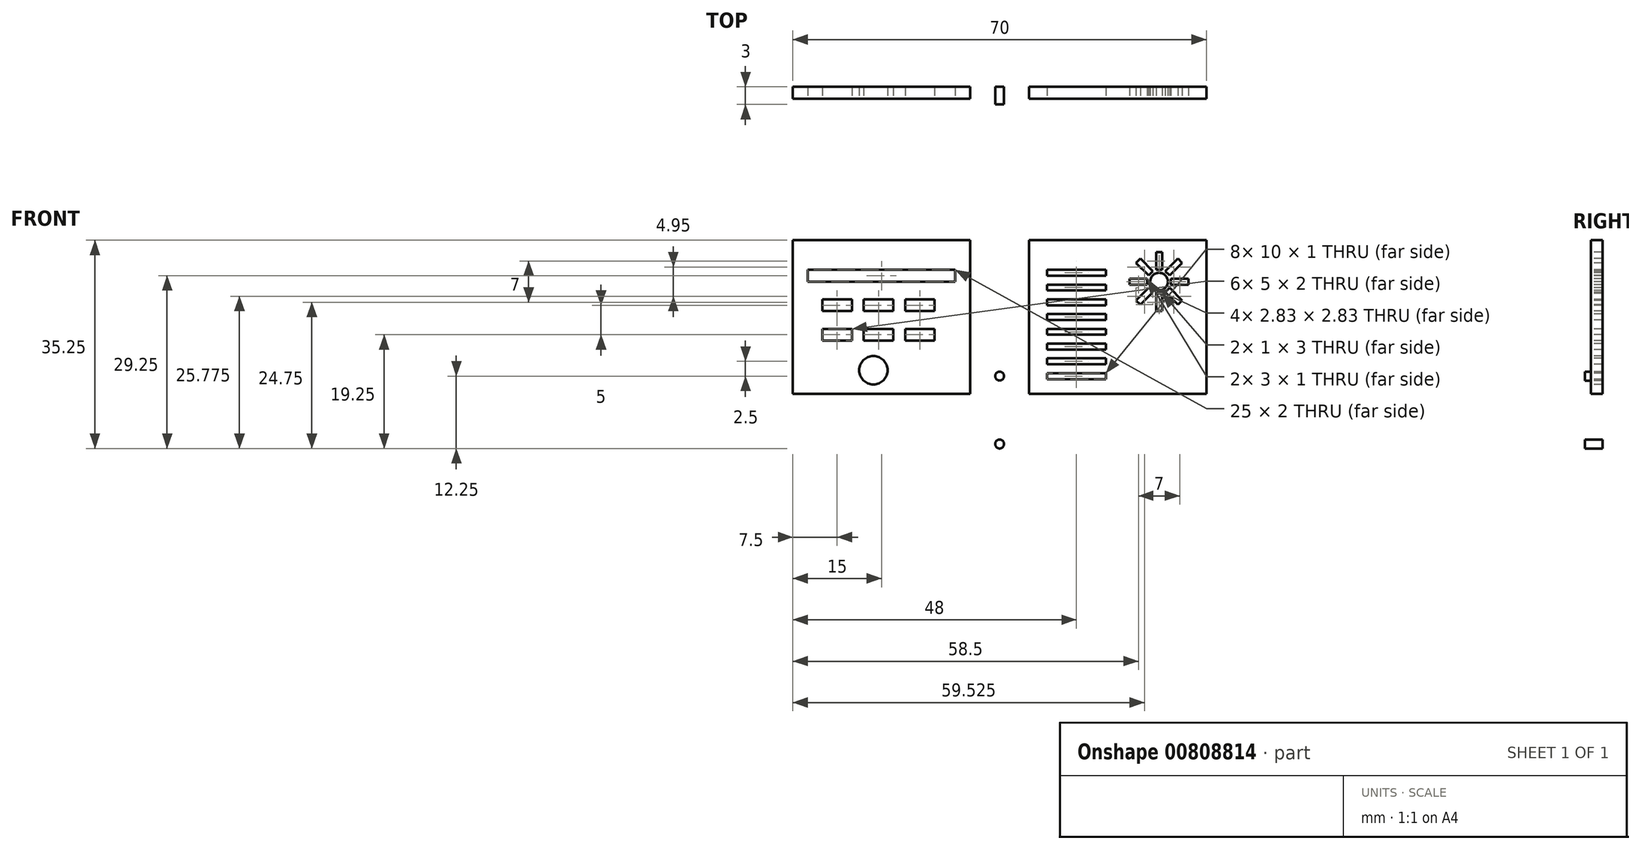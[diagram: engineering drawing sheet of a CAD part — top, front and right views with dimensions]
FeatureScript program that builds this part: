
annotation { "Feature Type Name" : "Feature", "Feature Type Description" : "" }
export const myFeature = defineFeature(function(context is Context, id is Id, definition is map)
    precondition{}
    {
        {
            var Q0;
            Q0=qCreatedBy(makeId("Front.planeOp"),FACE);
            var sketch = newSketch(context, id + "F0", { "sketchPlane" : qUnion([Q0])});
            skLineSegment(sketch, "E0.bottom", {"start": v(-55, 50) * mm, "end": v(55, 50) * mm});
            skLineSegment(sketch, "E0.top", {"start": v(-55, -50) * mm, "end": v(55, -50) * mm});
            skPoint(sketch, "E0.middle", {"position": v(0, 0) * mm});
            skLineSegment(sketch, "E1.bottom", {"start": v(5, 53) * mm, "end": v(-5, 53) * mm});
            skLineSegment(sketch, "E1.top", {"start": v(5, 47) * mm, "end": v(-5, 47) * mm});
            skLineSegment(sketch, "E1.left", {"start": v(5, 53) * mm, "end": v(5, 47) * mm});
            skLineSegment(sketch, "E1.right", {"start": v(-5, 53) * mm, "end": v(-5, 47) * mm});
            skPoint(sketch, "E1.middle", {"position": v(0, 50) * mm});
            skLineSegment(sketch, "E2.bottom", {"start": v(-25, 47) * mm, "end": v(-35, 47) * mm});
            skLineSegment(sketch, "E2.top", {"start": v(-25, 53) * mm, "end": v(-35, 53) * mm});
            skLineSegment(sketch, "E2.left", {"start": v(-25, 47) * mm, "end": v(-25, 53) * mm});
            skLineSegment(sketch, "E2.right", {"start": v(-35, 47) * mm, "end": v(-35, 53) * mm});
            skPoint(sketch, "E2.middle", {"position": v(-30, 50) * mm});
            skLineSegment(sketch, "E3.bottom", {"start": v(25, 47) * mm, "end": v(35, 47) * mm});
            skLineSegment(sketch, "E3.top", {"start": v(25, 53) * mm, "end": v(35, 53) * mm});
            skLineSegment(sketch, "E3.left", {"start": v(25, 47) * mm, "end": v(25, 53) * mm});
            skLineSegment(sketch, "E3.right", {"start": v(35, 47) * mm, "end": v(35, 53) * mm});
            skPoint(sketch, "E3.middle", {"position": v(30, 50) * mm});
            skPoint(sketch, "E4.center", {"position": v(-2.67, -2.67) * mm});
            skLineSegment(sketch, "E5", {"start": v(0, 0) * mm, "end": v(18.8, 0) * mm});
            skLineSegment(sketch, "E6", {"start": v(-55, 50) * mm, "end": v(-55, -50) * mm});
            skLineSegment(sketch, "E7", {"start": v(55, -50) * mm, "end": v(55, 50) * mm});
            skLineSegment(sketch, "E8.bottom", {"start": v(-58, 5) * mm, "end": v(-52, 5) * mm});
            skLineSegment(sketch, "E8.top", {"start": v(-58, -5) * mm, "end": v(-52, -5) * mm});
            skLineSegment(sketch, "E8.left", {"start": v(-58, 5) * mm, "end": v(-58, -5) * mm});
            skLineSegment(sketch, "E8.right", {"start": v(-52, 5) * mm, "end": v(-52, -5) * mm});
            skPoint(sketch, "E8.middle", {"position": v(-55, 0) * mm});
            skLineSegment(sketch, "E9.bottom", {"start": v(58, 5) * mm, "end": v(52, 5) * mm});
            skLineSegment(sketch, "E9.top", {"start": v(58, -5) * mm, "end": v(52, -5) * mm});
            skLineSegment(sketch, "E9.left", {"start": v(58, 5) * mm, "end": v(58, -5) * mm});
            skLineSegment(sketch, "E9.right", {"start": v(52, 5) * mm, "end": v(52, -5) * mm});
            skPoint(sketch, "E9.middle", {"position": v(55, 0) * mm});
            skLineSegment(sketch, "E10.0.1.0", {"start": v(-52, 35) * mm, "end": v(-52, 25) * mm});
            skLineSegment(sketch, "E10.0.1.1", {"start": v(-58, 35) * mm, "end": v(-52, 35) * mm});
            skLineSegment(sketch, "E10.0.1.2", {"start": v(-58, 35) * mm, "end": v(-58, 25) * mm});
            skLineSegment(sketch, "E10.0.1.3", {"start": v(-58, 25) * mm, "end": v(-52, 25) * mm});
            skLineSegment(sketch, "E10.0.1.4", {"start": v(58, 25) * mm, "end": v(52, 25) * mm});
            skLineSegment(sketch, "E10.0.1.5", {"start": v(58, 35) * mm, "end": v(58, 25) * mm});
            skLineSegment(sketch, "E10.0.1.6", {"start": v(58, 35) * mm, "end": v(52, 35) * mm});
            skLineSegment(sketch, "E10.0.1.7", {"start": v(52, 35) * mm, "end": v(52, 25) * mm});
            skLineSegment(sketch, "E10.direction1", {"start": v(-52, -5) * mm, "end": v(-27, -5) * mm, "construction": true});
            skLineSegment(sketch, "E11.0.1.0", {"start": v(-52, -25) * mm, "end": v(-52, -35) * mm});
            skLineSegment(sketch, "E11.0.1.1", {"start": v(-58, -25) * mm, "end": v(-52, -25) * mm});
            skLineSegment(sketch, "E11.0.1.2", {"start": v(-58, -25) * mm, "end": v(-58, -35) * mm});
            skLineSegment(sketch, "E11.0.1.3", {"start": v(-58, -35) * mm, "end": v(-52, -35) * mm});
            skLineSegment(sketch, "E11.0.1.4", {"start": v(58, -35) * mm, "end": v(52, -35) * mm});
            skLineSegment(sketch, "E11.0.1.5", {"start": v(58, -25) * mm, "end": v(58, -35) * mm});
            skLineSegment(sketch, "E11.0.1.6", {"start": v(58, -25) * mm, "end": v(52, -25) * mm});
            skLineSegment(sketch, "E11.0.1.7", {"start": v(52, -25) * mm, "end": v(52, -35) * mm});
            skLineSegment(sketch, "E11.direction2", {"start": v(-52, -5) * mm, "end": v(-52, -35) * mm, "construction": true});
            skLineSegment(sketch, "E12.MirrorCS", {"start": v(-25, -47) * mm, "end": v(-35, -47) * mm});
            skLineSegment(sketch, "E13.MirrorCS", {"start": v(-35, -47) * mm, "end": v(-35, -53) * mm});
            skLineSegment(sketch, "E14.MirrorCS", {"start": v(-25, -53) * mm, "end": v(-35, -53) * mm});
            skLineSegment(sketch, "E15.MirrorCS", {"start": v(-25, -47) * mm, "end": v(-25, -53) * mm});
            skLineSegment(sketch, "E16.MirrorCS", {"start": v(-5, -53) * mm, "end": v(-5, -47) * mm});
            skLineSegment(sketch, "E17.MirrorCS", {"start": v(5, -53) * mm, "end": v(-5, -53) * mm});
            skLineSegment(sketch, "E18.MirrorCS", {"start": v(5, -47) * mm, "end": v(-5, -47) * mm});
            skLineSegment(sketch, "E19.MirrorCS", {"start": v(5, -53) * mm, "end": v(5, -47) * mm});
            skLineSegment(sketch, "E20.MirrorCS", {"start": v(35, -47) * mm, "end": v(35, -53) * mm});
            skLineSegment(sketch, "E21.MirrorCS", {"start": v(25, -53) * mm, "end": v(35, -53) * mm});
            skLineSegment(sketch, "E22.MirrorCS", {"start": v(25, -47) * mm, "end": v(35, -47) * mm});
            skLineSegment(sketch, "E23.MirrorCS", {"start": v(25, -47) * mm, "end": v(25, -53) * mm});
            skSolve(sketch);
        }
        {
            var Q0;
            {var subQ5=sQuery(id+"F0.wireOp",EDGE,"E2.top");Q0=makeQuery(id+"F0.imprint","IMPRINT",FACE,{"disambiguationData":[TD([[makeQuery(id+"F0.imprint","IMPRINT",EDGE,{"derivedFrom":subQ5}),1.0]])]});}
            var Q1;
            {var subQ5=sQuery(id+"F0.wireOp",EDGE,"E1.bottom");Q1=makeQuery(id+"F0.imprint","IMPRINT",FACE,{"disambiguationData":[TD([[makeQuery(id+"F0.imprint","IMPRINT",EDGE,{"derivedFrom":subQ5}),1.0]])]});}
            var Q2;
            {var subQ5=sQuery(id+"F0.wireOp",EDGE,"E3.top");Q2=makeQuery(id+"F0.imprint","IMPRINT",FACE,{"disambiguationData":[TD([[makeQuery(id+"F0.imprint","IMPRINT",EDGE,{"derivedFrom":subQ5}),-1.0]])]});}
            var Q3;
            {var subQ5=sQuery(id+"F0.wireOp",EDGE,"E4.2.10");Q3=makeQuery(id+"F0.imprint","IMPRINT",FACE,{"disambiguationData":[TD([[makeQuery(id+"F0.imprint","IMPRINT",EDGE,{"derivedFrom":subQ5}),-1.0]])]});}
            var Q4;
            {var subQ5=sQuery(id+"F0.wireOp",EDGE,"E4.2.7");Q4=makeQuery(id+"F0.imprint","IMPRINT",FACE,{"disambiguationData":[TD([[makeQuery(id+"F0.imprint","IMPRINT",EDGE,{"derivedFrom":subQ5}),1.0]])]});}
            var Q5;
            {var subQ5=sQuery(id+"F0.wireOp",EDGE,"E4.2.2");Q5=makeQuery(id+"F0.imprint","IMPRINT",FACE,{"disambiguationData":[TD([[makeQuery(id+"F0.imprint","IMPRINT",EDGE,{"derivedFrom":subQ5}),1.0]])]});}
            var Q6;
            {var subQ5=sQuery(id+"F0.wireOp",EDGE,"E2.bottom");Q6=makeQuery(id+"F0.imprint","IMPRINT",FACE,{"disambiguationData":[TD([[makeQuery(id+"F0.imprint","IMPRINT",EDGE,{"derivedFrom":subQ5}),-1.0]])]});}
            var Q7;
            {var subQ5=sQuery(id+"F0.wireOp",EDGE,"E1.top");Q7=makeQuery(id+"F0.imprint","IMPRINT",FACE,{"disambiguationData":[TD([[makeQuery(id+"F0.imprint","IMPRINT",EDGE,{"derivedFrom":subQ5}),-1.0]])]});}
            var Q8;
            {var subQ5=sQuery(id+"F0.wireOp",EDGE,"E3.bottom");Q8=makeQuery(id+"F0.imprint","IMPRINT",FACE,{"disambiguationData":[TD([[makeQuery(id+"F0.imprint","IMPRINT",EDGE,{"derivedFrom":subQ5}),1.0]])]});}
            var Q9;
            {var subQ5=sQuery(id+"F0.wireOp",EDGE,"E4.2.9");Q9=makeQuery(id+"F0.imprint","IMPRINT",FACE,{"disambiguationData":[TD([[makeQuery(id+"F0.imprint","IMPRINT",EDGE,{"derivedFrom":subQ5}),1.0]])]});}
            var Q10;
            {var subQ5=sQuery(id+"F0.wireOp",EDGE,"E4.2.5");Q10=makeQuery(id+"F0.imprint","IMPRINT",FACE,{"disambiguationData":[TD([[makeQuery(id+"F0.imprint","IMPRINT",EDGE,{"derivedFrom":subQ5}),-1.0]])]});}
            var Q11;
            {var subQ5=sQuery(id+"F0.wireOp",EDGE,"E4.2.0");Q11=makeQuery(id+"F0.imprint","IMPRINT",FACE,{"disambiguationData":[TD([[makeQuery(id+"F0.imprint","IMPRINT",EDGE,{"derivedFrom":subQ5}),-1.0]])]});}
            var Q12;
            {var subQ65=sQuery(id+"F0.wireOp",EDGE,"E1.top");Q12=makeQuery(id+"F0.imprint","IMPRINT",FACE,{"disambiguationData":[TD([[makeQuery(id+"F0.imprint","IMPRINT",EDGE,{"derivedFrom":subQ65}),1.0]])]});}
            var Q13;
            {var subQ5=sQuery(id+"F0.wireOp",EDGE,"E22.MirrorCS");Q13=makeQuery(id+"F0.imprint","IMPRINT",FACE,{"disambiguationData":[TD([[makeQuery(id+"F0.imprint","IMPRINT",EDGE,{"derivedFrom":subQ5}),-1.0]])]});}
            var Q14;
            {var subQ5=sQuery(id+"F0.wireOp",EDGE,"E21.MirrorCS");Q14=makeQuery(id+"F0.imprint","IMPRINT",FACE,{"disambiguationData":[TD([[makeQuery(id+"F0.imprint","IMPRINT",EDGE,{"derivedFrom":subQ5}),1.0]])]});}
            var Q15;
            {var subQ5=sQuery(id+"F0.wireOp",EDGE,"E18.MirrorCS");Q15=makeQuery(id+"F0.imprint","IMPRINT",FACE,{"disambiguationData":[TD([[makeQuery(id+"F0.imprint","IMPRINT",EDGE,{"derivedFrom":subQ5}),1.0]])]});}
            var Q16;
            {var subQ5=sQuery(id+"F0.wireOp",EDGE,"E17.MirrorCS");Q16=makeQuery(id+"F0.imprint","IMPRINT",FACE,{"disambiguationData":[TD([[makeQuery(id+"F0.imprint","IMPRINT",EDGE,{"derivedFrom":subQ5}),-1.0]])]});}
            var Q17;
            {var subQ5=sQuery(id+"F0.wireOp",EDGE,"E12.MirrorCS");Q17=makeQuery(id+"F0.imprint","IMPRINT",FACE,{"disambiguationData":[TD([[makeQuery(id+"F0.imprint","IMPRINT",EDGE,{"derivedFrom":subQ5}),1.0]])]});}
            var Q18;
            {var subQ5=sQuery(id+"F0.wireOp",EDGE,"E14.MirrorCS");Q18=makeQuery(id+"F0.imprint","IMPRINT",FACE,{"disambiguationData":[TD([[makeQuery(id+"F0.imprint","IMPRINT",EDGE,{"derivedFrom":subQ5}),-1.0]])]});}
            extrude(context, id + "F1", {"entities" : qUnion([Q0, Q1, Q2, Q3, Q4, Q5, Q6, Q7, Q8, Q9, Q10, Q11, Q12, Q13, Q14, Q15, Q16, Q17, Q18]), "depth" : 3 * mm, "offsetDistance" : 25 * mm});
        }
        {
            var Q0;
            Q0=makeQuery(id+"F1.opExtrude","CAP_FACE",FACE,{"disambiguationData":[OSD([sQuery(id+"F0.wireOp",EDGE,"E0.bottom"),sQuery(id+"F0.wireOp",EDGE,"E0.top"),sQuery(id+"F0.wireOp",EDGE,"E0.left"),sQuery(id+"F0.wireOp",EDGE,"E0.right"),sQuery(id+"F0.wireOp",EDGE,"E1.bottom"),sQuery(id+"F0.wireOp",EDGE,"E1.left"),sQuery(id+"F0.wireOp",EDGE,"E1.right"),sQuery(id+"F0.wireOp",EDGE,"E2.top"),sQuery(id+"F0.wireOp",EDGE,"E2.left"),sQuery(id+"F0.wireOp",EDGE,"E2.right"),sQuery(id+"F0.wireOp",EDGE,"E3.top"),sQuery(id+"F0.wireOp",EDGE,"E3.left"),sQuery(id+"F0.wireOp",EDGE,"E3.right"),sQuery(id+"F0.wireOp",EDGE,"E4.1.0"),sQuery(id+"F0.wireOp",EDGE,"E4.1.1"),sQuery(id+"F0.wireOp",EDGE,"E4.1.3"),sQuery(id+"F0.wireOp",EDGE,"E4.1.4"),sQuery(id+"F0.wireOp",EDGE,"E4.1.5"),sQuery(id+"F0.wireOp",EDGE,"E4.1.6"),sQuery(id+"F0.wireOp",EDGE,"E4.1.8"),sQuery(id+"F0.wireOp",EDGE,"E4.1.9"),sQuery(id+"F0.wireOp",EDGE,"E4.1.11"),sQuery(id+"F0.wireOp",EDGE,"E4.2.1"),sQuery(id+"F0.wireOp",EDGE,"E4.2.2"),sQuery(id+"F0.wireOp",EDGE,"E4.2.3"),sQuery(id+"F0.wireOp",EDGE,"E4.2.4"),sQuery(id+"F0.wireOp",EDGE,"E4.2.6"),sQuery(id+"F0.wireOp",EDGE,"E4.2.7"),sQuery(id+"F0.wireOp",EDGE,"E4.2.8"),sQuery(id+"F0.wireOp",EDGE,"E4.2.10"),sQuery(id+"F0.wireOp",EDGE,"E4.2.11"),sQuery(id+"F0.wireOp",EDGE,"E4.3.0"),sQuery(id+"F0.wireOp",EDGE,"E4.3.1"),sQuery(id+"F0.wireOp",EDGE,"E4.3.3"),sQuery(id+"F0.wireOp",EDGE,"E4.3.4"),sQuery(id+"F0.wireOp",EDGE,"E4.3.5"),sQuery(id+"F0.wireOp",EDGE,"E4.3.6"),sQuery(id+"F0.wireOp",EDGE,"E4.3.8"),sQuery(id+"F0.wireOp",EDGE,"E4.3.9"),sQuery(id+"F0.wireOp",EDGE,"E4.3.11")])],"isStart":false});
            var sketch = newSketch(context, id + "F2", { "sketchPlane" : qUnion([Q0])});
            skLineSegment(sketch, "E24.bottom", {"start": v(-42, 10) * mm, "end": v(42, 10) * mm});
            skLineSegment(sketch, "E24.top", {"start": v(-42, -45) * mm, "end": v(42, -45) * mm});
            skLineSegment(sketch, "E24.left", {"start": v(-42, 10) * mm, "end": v(-42, -45) * mm});
            skLineSegment(sketch, "E24.right", {"start": v(42, 10) * mm, "end": v(42, -45) * mm});
            skCircle(sketch, "E25", {"center": v(0, 3.5) * mm, "radius": 0.75 * mm});
            skCircle(sketch, "E26", {"center": v(0, 15) * mm, "radius": 0.75 * mm});
            skLineSegment(sketch, "E27.bottom", {"start": v(-35, 10) * mm, "end": v(-5, 10) * mm});
            skLineSegment(sketch, "E27.top", {"start": v(-35, 38) * mm, "end": v(-5, 38) * mm});
            skLineSegment(sketch, "E27.left", {"start": v(-35, 12) * mm, "end": v(-35, 38) * mm});
            skLineSegment(sketch, "E27.right", {"start": v(-5, 12) * mm, "end": v(-5, 38) * mm});
            skLineSegment(sketch, "E28.bottom", {"start": v(35, 10) * mm, "end": v(5, 10) * mm});
            skLineSegment(sketch, "E28.top", {"start": v(35, 38) * mm, "end": v(5, 38) * mm});
            skLineSegment(sketch, "E28.left", {"start": v(35, 12) * mm, "end": v(35, 38) * mm});
            skLineSegment(sketch, "E28.right", {"start": v(5, 12) * mm, "end": v(5, 38) * mm});
            skLineSegment(sketch, "E29.bottom", {"start": v(-32.5, 33) * mm, "end": v(-7.5, 33) * mm});
            skLineSegment(sketch, "E29.top", {"start": v(-32.5, 31) * mm, "end": v(-7.5, 31) * mm});
            skLineSegment(sketch, "E29.left", {"start": v(-32.5, 33) * mm, "end": v(-32.5, 31) * mm});
            skLineSegment(sketch, "E29.right", {"start": v(-7.5, 33) * mm, "end": v(-7.5, 31) * mm});
            skLineSegment(sketch, "E30.bottom", {"start": v(-30, 28) * mm, "end": v(-25, 28) * mm});
            skLineSegment(sketch, "E30.top", {"start": v(-30, 26) * mm, "end": v(-25, 26) * mm});
            skLineSegment(sketch, "E30.left", {"start": v(-30, 28) * mm, "end": v(-30, 26) * mm});
            skLineSegment(sketch, "E30.right", {"start": v(-25, 28) * mm, "end": v(-25, 26) * mm});
            skCircle(sketch, "E31", {"center": v(-21.37, 16) * mm, "radius": 2.4 * mm});
            skLineSegment(sketch, "E32.0.1.0", {"start": v(-30, 23) * mm, "end": v(-25, 23) * mm});
            skLineSegment(sketch, "E32.0.1.1", {"start": v(-30, 21) * mm, "end": v(-25, 21) * mm});
            skLineSegment(sketch, "E32.0.1.2", {"start": v(-25, 23) * mm, "end": v(-25, 21) * mm});
            skLineSegment(sketch, "E32.0.1.3", {"start": v(-30, 23) * mm, "end": v(-30, 21) * mm});
            skLineSegment(sketch, "E32.1.0.0", {"start": v(-23, 28) * mm, "end": v(-18, 28) * mm});
            skLineSegment(sketch, "E32.1.0.1", {"start": v(-23, 26) * mm, "end": v(-18, 26) * mm});
            skLineSegment(sketch, "E32.1.0.2", {"start": v(-18, 28) * mm, "end": v(-18, 26) * mm});
            skLineSegment(sketch, "E32.1.0.3", {"start": v(-23, 28) * mm, "end": v(-23, 26) * mm});
            skLineSegment(sketch, "E32.1.1.0", {"start": v(-23, 23) * mm, "end": v(-18, 23) * mm});
            skLineSegment(sketch, "E32.1.1.1", {"start": v(-23, 21) * mm, "end": v(-18, 21) * mm});
            skLineSegment(sketch, "E32.1.1.2", {"start": v(-18, 23) * mm, "end": v(-18, 21) * mm});
            skLineSegment(sketch, "E32.1.1.3", {"start": v(-23, 23) * mm, "end": v(-23, 21) * mm});
            skLineSegment(sketch, "E32.2.0.0", {"start": v(-16, 28) * mm, "end": v(-11, 28) * mm});
            skLineSegment(sketch, "E32.2.0.1", {"start": v(-16, 26) * mm, "end": v(-11, 26) * mm});
            skLineSegment(sketch, "E32.2.0.2", {"start": v(-11, 28) * mm, "end": v(-11, 26) * mm});
            skLineSegment(sketch, "E32.2.0.3", {"start": v(-16, 28) * mm, "end": v(-16, 26) * mm});
            skLineSegment(sketch, "E32.2.1.0", {"start": v(-16, 23) * mm, "end": v(-11, 23) * mm});
            skLineSegment(sketch, "E32.2.1.1", {"start": v(-16, 21) * mm, "end": v(-11, 21) * mm});
            skLineSegment(sketch, "E32.2.1.2", {"start": v(-11, 23) * mm, "end": v(-11, 21) * mm});
            skLineSegment(sketch, "E32.2.1.3", {"start": v(-16, 23) * mm, "end": v(-16, 21) * mm});
            skLineSegment(sketch, "E32.direction1", {"start": v(-30, 28) * mm, "end": v(-23, 28) * mm, "construction": true});
            skLineSegment(sketch, "E32.direction2", {"start": v(-30, 28) * mm, "end": v(-30, 23) * mm, "construction": true});
            skLineSegment(sketch, "E33", {"start": v(-35, 12) * mm, "end": v(-5, 12) * mm});
            skLineSegment(sketch, "E34.bottom", {"start": v(8, 33) * mm, "end": v(18, 33) * mm});
            skLineSegment(sketch, "E34.top", {"start": v(8, 32) * mm, "end": v(18, 32) * mm});
            skLineSegment(sketch, "E34.left", {"start": v(8, 33) * mm, "end": v(8, 32) * mm});
            skLineSegment(sketch, "E34.right", {"start": v(18, 33) * mm, "end": v(18, 32) * mm});
            skCircle(sketch, "E35", {"center": v(27, 31) * mm, "radius": 2 * mm});
            skLineSegment(sketch, "E36.bottom", {"start": v(26.5, 29) * mm, "end": v(27.5, 29) * mm});
            skLineSegment(sketch, "E36.top", {"start": v(26.5, 26) * mm, "end": v(27.5, 26) * mm});
            skLineSegment(sketch, "E36.left", {"start": v(26.5, 29) * mm, "end": v(26.5, 26) * mm});
            skLineSegment(sketch, "E36.right", {"start": v(27.5, 29) * mm, "end": v(27.5, 26) * mm});
            skLineSegment(sketch, "E37.0.1.0", {"start": v(8, 30.5) * mm, "end": v(18, 30.5) * mm});
            skLineSegment(sketch, "E37.0.1.1", {"start": v(8, 29.5) * mm, "end": v(18, 29.5) * mm});
            skLineSegment(sketch, "E37.0.1.2", {"start": v(18, 30.5) * mm, "end": v(18, 29.5) * mm});
            skLineSegment(sketch, "E37.0.1.3", {"start": v(8, 30.5) * mm, "end": v(8, 29.5) * mm});
            skLineSegment(sketch, "E37.0.2.0", {"start": v(8, 28) * mm, "end": v(18, 28) * mm});
            skLineSegment(sketch, "E37.0.2.1", {"start": v(8, 27) * mm, "end": v(18, 27) * mm});
            skLineSegment(sketch, "E37.0.2.2", {"start": v(18, 28) * mm, "end": v(18, 27) * mm});
            skLineSegment(sketch, "E37.0.2.3", {"start": v(8, 28) * mm, "end": v(8, 27) * mm});
            skLineSegment(sketch, "E37.0.3.0", {"start": v(8, 25.5) * mm, "end": v(18, 25.5) * mm});
            skLineSegment(sketch, "E37.0.3.1", {"start": v(8, 24.5) * mm, "end": v(18, 24.5) * mm});
            skLineSegment(sketch, "E37.0.3.2", {"start": v(18, 25.5) * mm, "end": v(18, 24.5) * mm});
            skLineSegment(sketch, "E37.0.3.3", {"start": v(8, 25.5) * mm, "end": v(8, 24.5) * mm});
            skLineSegment(sketch, "E37.0.4.0", {"start": v(8, 23) * mm, "end": v(18, 23) * mm});
            skLineSegment(sketch, "E37.0.4.1", {"start": v(8, 22) * mm, "end": v(18, 22) * mm});
            skLineSegment(sketch, "E37.0.4.2", {"start": v(18, 23) * mm, "end": v(18, 22) * mm});
            skLineSegment(sketch, "E37.0.4.3", {"start": v(8, 23) * mm, "end": v(8, 22) * mm});
            skLineSegment(sketch, "E37.0.5.0", {"start": v(8, 20.5) * mm, "end": v(18, 20.5) * mm});
            skLineSegment(sketch, "E37.0.5.1", {"start": v(8, 19.5) * mm, "end": v(18, 19.5) * mm});
            skLineSegment(sketch, "E37.0.5.2", {"start": v(18, 20.5) * mm, "end": v(18, 19.5) * mm});
            skLineSegment(sketch, "E37.0.5.3", {"start": v(8, 20.5) * mm, "end": v(8, 19.5) * mm});
            skLineSegment(sketch, "E37.0.6.0", {"start": v(8, 18) * mm, "end": v(18, 18) * mm});
            skLineSegment(sketch, "E37.0.6.1", {"start": v(8, 17) * mm, "end": v(18, 17) * mm});
            skLineSegment(sketch, "E37.0.6.2", {"start": v(18, 18) * mm, "end": v(18, 17) * mm});
            skLineSegment(sketch, "E37.0.6.3", {"start": v(8, 18) * mm, "end": v(8, 17) * mm});
            skLineSegment(sketch, "E37.0.7.0", {"start": v(8, 15.5) * mm, "end": v(18, 15.5) * mm});
            skLineSegment(sketch, "E37.0.7.1", {"start": v(8, 14.5) * mm, "end": v(18, 14.5) * mm});
            skLineSegment(sketch, "E37.0.7.2", {"start": v(18, 15.5) * mm, "end": v(18, 14.5) * mm});
            skLineSegment(sketch, "E37.0.7.3", {"start": v(8, 15.5) * mm, "end": v(8, 14.5) * mm});
            skLineSegment(sketch, "E37.direction1", {"start": v(8, 33) * mm, "end": v(33, 33) * mm, "construction": true});
            skLineSegment(sketch, "E37.direction2", {"start": v(8, 33) * mm, "end": v(8, 30.5) * mm, "construction": true});
            skCircle(sketch, "E38", {"center": v(27, 31) * mm, "radius": 1.5 * mm});
            skLineSegment(sketch, "E39.1.2", {"start": v(-38.36, 8.45) * mm, "end": v(-35.77, 9.95) * mm});
            skLineSegment(sketch, "E39.2.0", {"start": v(11.36, -38.32) * mm, "end": v(8.77, -36.82) * mm});
            skLineSegment(sketch, "E39.2.1", {"start": v(9.27, -35.95) * mm, "end": v(8.77, -36.82) * mm});
            skLineSegment(sketch, "E39.2.2", {"start": v(11.86, -37.45) * mm, "end": v(9.27, -35.95) * mm});
            skPoint(sketch, "E39.center", {"position": v(0, 0) * mm});
            skLineSegment(sketch, "E40.1.1", {"start": v(28.77, 29.94) * mm, "end": v(30.89, 27.82) * mm});
            skLineSegment(sketch, "E40.1.2", {"start": v(30.18, 27.11) * mm, "end": v(30.89, 27.82) * mm});
            skLineSegment(sketch, "E40.1.3", {"start": v(28.06, 29.23) * mm, "end": v(30.18, 27.11) * mm});
            skLineSegment(sketch, "E40.1.4", {"start": v(28.06, 29.23) * mm, "end": v(28.77, 29.94) * mm});
            skLineSegment(sketch, "E40.2.1", {"start": v(29, 31.5) * mm, "end": v(32, 31.5) * mm});
            skLineSegment(sketch, "E40.2.2", {"start": v(32, 30.5) * mm, "end": v(32, 31.5) * mm});
            skLineSegment(sketch, "E40.2.3", {"start": v(29, 30.5) * mm, "end": v(32, 30.5) * mm});
            skLineSegment(sketch, "E40.2.4", {"start": v(29, 30.5) * mm, "end": v(29, 31.5) * mm});
            skLineSegment(sketch, "E40.3.1", {"start": v(28.06, 32.77) * mm, "end": v(30.18, 34.89) * mm});
            skLineSegment(sketch, "E40.3.2", {"start": v(30.89, 34.18) * mm, "end": v(30.18, 34.89) * mm});
            skLineSegment(sketch, "E40.3.3", {"start": v(28.77, 32.06) * mm, "end": v(30.89, 34.18) * mm});
            skLineSegment(sketch, "E40.3.4", {"start": v(28.77, 32.06) * mm, "end": v(28.06, 32.77) * mm});
            skLineSegment(sketch, "E40.4.1", {"start": v(26.5, 33) * mm, "end": v(26.5, 36) * mm});
            skLineSegment(sketch, "E40.4.2", {"start": v(27.5, 36) * mm, "end": v(26.5, 36) * mm});
            skLineSegment(sketch, "E40.4.3", {"start": v(27.5, 33) * mm, "end": v(27.5, 36) * mm});
            skLineSegment(sketch, "E40.4.4", {"start": v(27.5, 33) * mm, "end": v(26.5, 33) * mm});
            skLineSegment(sketch, "E40.5.1", {"start": v(25.23, 32.06) * mm, "end": v(23.11, 34.18) * mm});
            skLineSegment(sketch, "E40.5.2", {"start": v(23.82, 34.89) * mm, "end": v(23.11, 34.18) * mm});
            skLineSegment(sketch, "E40.5.3", {"start": v(25.94, 32.77) * mm, "end": v(23.82, 34.89) * mm});
            skLineSegment(sketch, "E40.5.4", {"start": v(25.94, 32.77) * mm, "end": v(25.23, 32.06) * mm});
            skLineSegment(sketch, "E40.6.1", {"start": v(25, 30.5) * mm, "end": v(22, 30.5) * mm});
            skLineSegment(sketch, "E40.6.2", {"start": v(22, 31.5) * mm, "end": v(22, 30.5) * mm});
            skLineSegment(sketch, "E40.6.3", {"start": v(25, 31.5) * mm, "end": v(22, 31.5) * mm});
            skLineSegment(sketch, "E40.6.4", {"start": v(25, 31.5) * mm, "end": v(25, 30.5) * mm});
            skLineSegment(sketch, "E40.7.1", {"start": v(25.94, 29.23) * mm, "end": v(23.82, 27.11) * mm});
            skLineSegment(sketch, "E40.7.2", {"start": v(23.11, 27.82) * mm, "end": v(23.82, 27.11) * mm});
            skLineSegment(sketch, "E40.7.3", {"start": v(25.23, 29.94) * mm, "end": v(23.11, 27.82) * mm});
            skLineSegment(sketch, "E40.7.4", {"start": v(25.23, 29.94) * mm, "end": v(25.94, 29.23) * mm});
            skLineSegment(sketch, "E41", {"start": v(5, 12) * mm, "end": v(35, 12) * mm});
            skSolve(sketch);
        }
        {
            var Q0;
            Q0=makeQuery(id+"F2.imprint","IMPRINT",FACE,{"disambiguationData":[TD([[makeQuery(id+"F2.imprint","IMPRINT",EDGE,{"derivedFrom":sQuery(id+"F2.wireOp",EDGE,"E26")}),-1.0]])]});
            var Q1;
            Q1=makeQuery(id+"F2.imprint","IMPRINT",FACE,{"disambiguationData":[TD([[makeQuery(id+"F2.imprint","IMPRINT",EDGE,{"derivedFrom":sQuery(id+"F2.wireOp",EDGE,"E32.2.1.0")}),-1.0]])]});
            var Q2;
            Q2=makeQuery(id+"F2.imprint","IMPRINT",FACE,{"disambiguationData":[TD([[makeQuery(id+"F2.imprint","IMPRINT",EDGE,{"derivedFrom":sQuery(id+"F2.wireOp",EDGE,"E32.1.1.0")}),-1.0]])]});
            var Q3;
            Q3=makeQuery(id+"F2.imprint","IMPRINT",FACE,{"disambiguationData":[TD([[makeQuery(id+"F2.imprint","IMPRINT",EDGE,{"derivedFrom":sQuery(id+"F2.wireOp",EDGE,"E31")}),1.0]])]});
            var Q4;
            Q4=makeQuery(id+"F2.imprint","IMPRINT",FACE,{"disambiguationData":[TD([[makeQuery(id+"F2.imprint","IMPRINT",EDGE,{"derivedFrom":sQuery(id+"F2.wireOp",EDGE,"E32.0.1.0")}),-1.0]])]});
            var Q5;
            Q5=makeQuery(id+"F2.imprint","IMPRINT",FACE,{"disambiguationData":[TD([[makeQuery(id+"F2.imprint","IMPRINT",EDGE,{"derivedFrom":sQuery(id+"F2.wireOp",EDGE,"E30.bottom")}),-1.0]])]});
            var Q6;
            Q6=makeQuery(id+"F2.imprint","IMPRINT",FACE,{"disambiguationData":[TD([[makeQuery(id+"F2.imprint","IMPRINT",EDGE,{"derivedFrom":sQuery(id+"F2.wireOp",EDGE,"E32.1.0.0")}),-1.0]])]});
            var Q7;
            Q7=makeQuery(id+"F2.imprint","IMPRINT",FACE,{"disambiguationData":[TD([[makeQuery(id+"F2.imprint","IMPRINT",EDGE,{"derivedFrom":sQuery(id+"F2.wireOp",EDGE,"E32.2.0.0")}),-1.0]])]});
            var Q8;
            Q8=makeQuery(id+"F2.imprint","IMPRINT",FACE,{"disambiguationData":[TD([[makeQuery(id+"F2.imprint","IMPRINT",EDGE,{"derivedFrom":sQuery(id+"F2.wireOp",EDGE,"E29.bottom")}),-1.0]])]});
            var Q9;
            Q9=makeQuery(id+"F2.imprint","IMPRINT",FACE,{"disambiguationData":[TD([[makeQuery(id+"F2.imprint","IMPRINT",EDGE,{"derivedFrom":sQuery(id+"F2.wireOp",EDGE,"E34.bottom")}),-1.0]])]});
            var Q10;
            Q10=makeQuery(id+"F2.imprint","IMPRINT",FACE,{"disambiguationData":[TD([[makeQuery(id+"F2.imprint","IMPRINT",EDGE,{"derivedFrom":sQuery(id+"F2.wireOp",EDGE,"E37.0.1.0")}),-1.0]])]});
            var Q11;
            Q11=makeQuery(id+"F2.imprint","IMPRINT",FACE,{"disambiguationData":[TD([[makeQuery(id+"F2.imprint","IMPRINT",EDGE,{"derivedFrom":sQuery(id+"F2.wireOp",EDGE,"E37.0.2.0")}),-1.0]])]});
            var Q12;
            Q12=makeQuery(id+"F2.imprint","IMPRINT",FACE,{"disambiguationData":[TD([[makeQuery(id+"F2.imprint","IMPRINT",EDGE,{"derivedFrom":sQuery(id+"F2.wireOp",EDGE,"E37.0.3.0")}),-1.0]])]});
            var Q13;
            Q13=makeQuery(id+"F2.imprint","IMPRINT",FACE,{"disambiguationData":[TD([[makeQuery(id+"F2.imprint","IMPRINT",EDGE,{"derivedFrom":sQuery(id+"F2.wireOp",EDGE,"E37.0.4.0")}),-1.0]])]});
            var Q14;
            Q14=makeQuery(id+"F2.imprint","IMPRINT",FACE,{"disambiguationData":[TD([[makeQuery(id+"F2.imprint","IMPRINT",EDGE,{"derivedFrom":sQuery(id+"F2.wireOp",EDGE,"E37.0.5.0")}),-1.0]])]});
            var Q15;
            Q15=makeQuery(id+"F2.imprint","IMPRINT",FACE,{"disambiguationData":[TD([[makeQuery(id+"F2.imprint","IMPRINT",EDGE,{"derivedFrom":sQuery(id+"F2.wireOp",EDGE,"E37.0.6.0")}),-1.0]])]});
            var Q16;
            Q16=makeQuery(id+"F2.imprint","IMPRINT",FACE,{"disambiguationData":[TD([[makeQuery(id+"F2.imprint","IMPRINT",EDGE,{"derivedFrom":sQuery(id+"F2.wireOp",EDGE,"E37.0.7.0")}),-1.0]])]});
            var Q17;
            Q17=makeQuery(id+"F2.imprint","IMPRINT",FACE,{"disambiguationData":[TD([[makeQuery(id+"F2.imprint","IMPRINT",EDGE,{"derivedFrom":sQuery(id+"F2.wireOp",EDGE,"E25")}),-1.0]])]});
            var Q18;
            {var subQ3=sQuery(id+"F2.wireOp",EDGE,"E40.3.1");Q18=makeQuery(id+"F2.imprint","IMPRINT",FACE,{"disambiguationData":[TD([[makeQuery(id+"F2.imprint","IMPRINT",EDGE,{"derivedFrom":subQ3}),-1.0]])]});}
            var Q19;
            {var subQ3=sQuery(id+"F2.wireOp",EDGE,"E40.4.1");Q19=makeQuery(id+"F2.imprint","IMPRINT",FACE,{"disambiguationData":[TD([[makeQuery(id+"F2.imprint","IMPRINT",EDGE,{"derivedFrom":subQ3}),-1.0]])]});}
            var Q20;
            {var subQ3=sQuery(id+"F2.wireOp",EDGE,"E40.5.1");Q20=makeQuery(id+"F2.imprint","IMPRINT",FACE,{"disambiguationData":[TD([[makeQuery(id+"F2.imprint","IMPRINT",EDGE,{"derivedFrom":subQ3}),-1.0]])]});}
            var Q21;
            {var subQ3=sQuery(id+"F2.wireOp",EDGE,"E40.6.1");Q21=makeQuery(id+"F2.imprint","IMPRINT",FACE,{"disambiguationData":[TD([[makeQuery(id+"F2.imprint","IMPRINT",EDGE,{"derivedFrom":subQ3}),-1.0]])]});}
            var Q22;
            {var subQ3=sQuery(id+"F2.wireOp",EDGE,"E40.7.1");Q22=makeQuery(id+"F2.imprint","IMPRINT",FACE,{"disambiguationData":[TD([[makeQuery(id+"F2.imprint","IMPRINT",EDGE,{"derivedFrom":subQ3}),-1.0]])]});}
            var Q23;
            Q23=makeQuery(id+"F2.imprint","IMPRINT",FACE,{"disambiguationData":[TD([[makeQuery(id+"F2.imprint","IMPRINT",EDGE,{"derivedFrom":sQuery(id+"F2.wireOp",EDGE,"E36.top")}),1.0]])]});
            var Q24;
            {var subQ3=sQuery(id+"F2.wireOp",EDGE,"E40.1.1");Q24=makeQuery(id+"F2.imprint","IMPRINT",FACE,{"disambiguationData":[TD([[makeQuery(id+"F2.imprint","IMPRINT",EDGE,{"derivedFrom":subQ3}),-1.0]])]});}
            var Q25;
            {var subQ3=sQuery(id+"F2.wireOp",EDGE,"E40.2.1");Q25=makeQuery(id+"F2.imprint","IMPRINT",FACE,{"disambiguationData":[TD([[makeQuery(id+"F2.imprint","IMPRINT",EDGE,{"derivedFrom":subQ3}),-1.0]])]});}
            var Q26;
            Q26=makeQuery(id+"F2.imprint","IMPRINT",FACE,{"disambiguationData":[TD([[makeQuery(id+"F2.imprint","IMPRINT",EDGE,{"derivedFrom":sQuery(id+"F2.wireOp",EDGE,"E38")}),1.0]])]});
            extrude(context, id + "F3", {"entities" : qUnion([Q0, Q1, Q2, Q3, Q4, Q5, Q6, Q7, Q8, Q9, Q10, Q11, Q12, Q13, Q14, Q15, Q16, Q17, Q18, Q19, Q20, Q21, Q22, Q23, Q24, Q25, Q26]), "operationType" : NewBodyOperationType.REMOVE, "oppositeDirection" : true, "depth" : 3 * mm, "offsetDistance" : 25 * mm});
        }
        {
            var Q0;
            Q0=makeQuery(id+"F2.imprint","IMPRINT",FACE,{"disambiguationData":[TD([[makeQuery(id+"F2.imprint","IMPRINT",EDGE,{"derivedFrom":sQuery(id+"F2.wireOp",EDGE,"E28.top")}),1.0]])]});
            var Q1;
            Q1=makeQuery(id+"F2.imprint","IMPRINT",FACE,{"disambiguationData":[TD([[makeQuery(id+"F2.imprint","IMPRINT",EDGE,{"derivedFrom":sQuery(id+"F2.wireOp",EDGE,"E27.top")}),-1.0]])]});
            var Q2;
            Q2=makeQuery(id+"F2.imprint","IMPRINT",FACE,{"disambiguationData":[TD([[makeQuery(id+"F2.imprint","IMPRINT",EDGE,{"derivedFrom":sQuery(id+"F2.wireOp",EDGE,"E38")}),-1.0]])]});
            var Q3;
            Q3=makeQuery(id+"F2.imprint","IMPRINT",FACE,{"disambiguationData":[TD([[makeQuery(id+"F2.imprint","IMPRINT",EDGE,{"derivedFrom":sQuery(id+"F2.wireOp",EDGE,"E24.top")}),1.0]])]});
            var Q4;
            {var subQ0=sQuery(id+"F2.wireOp",EDGE,"E39.1.2");Q4=makeQuery(id+"F2.imprint","IMPRINT",FACE,{"disambiguationData":[TD([[makeQuery(id+"F2.imprint","IMPRINT",EDGE,{"derivedFrom":subQ0}),1.0]])]});}
            var Q5;
            Q5=makeQuery(id+"F2.imprint","IMPRINT",FACE,{"disambiguationData":[TD([[makeQuery(id+"F2.imprint","IMPRINT",EDGE,{"derivedFrom":sQuery(id+"F2.wireOp",EDGE,"E39.2.0")}),-1.0]])]});
            var Q6;
            Q6=sQuery(id+"F2.wireOp",EDGE,"E24.right");
            var Q7;
            Q7=sQuery(id+"F2.wireOp",EDGE,"E24.bottom");
            var Q8;
            Q8=sQuery(id+"F2.wireOp",EDGE,"E24.top");
            var Q9;
            Q9=sQuery(id+"F2.wireOp",EDGE,"E24.left");
            extrude(context, id + "F4", {"entities" : qUnion([Q0, Q1, Q2, Q3, Q4, Q5]), "operationType" : NewBodyOperationType.REMOVE, "surfaceEntities" : qUnion([Q6, Q7, Q8, Q9]), "oppositeDirection" : true, "depth" : 1 * mm, "offsetDistance" : 25 * mm});
        }
    });
